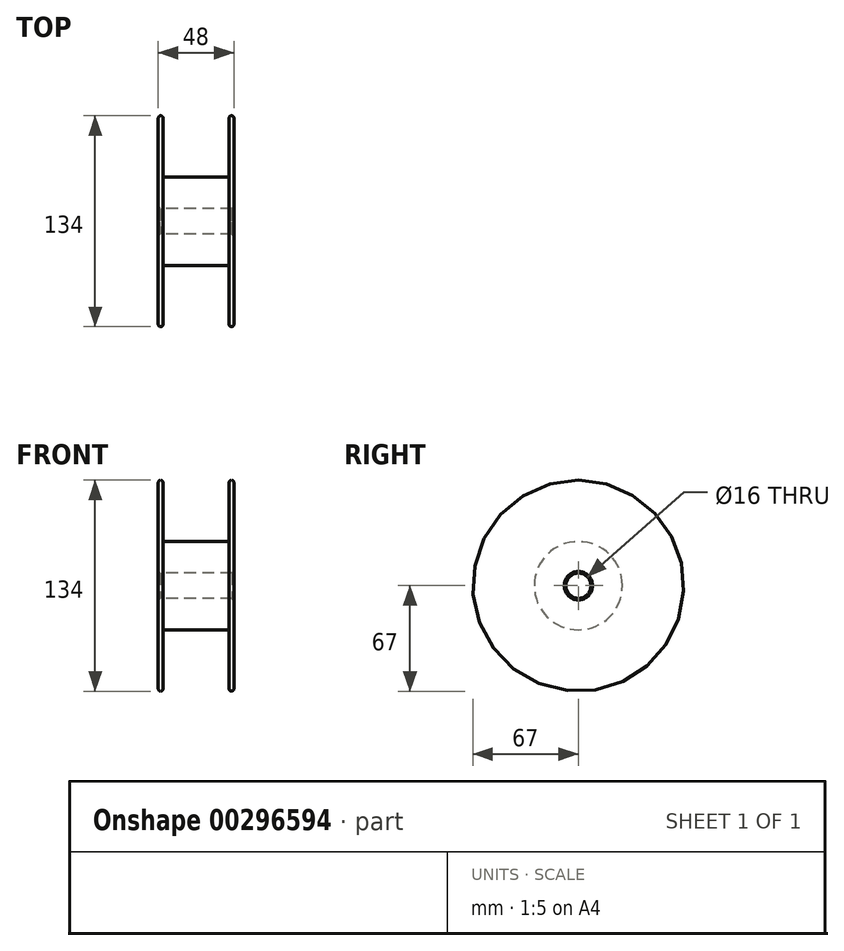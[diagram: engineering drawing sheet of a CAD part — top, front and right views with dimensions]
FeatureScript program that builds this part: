
annotation { "Feature Type Name" : "Feature", "Feature Type Description" : "" }
export const myFeature = defineFeature(function(context is Context, id is Id, definition is map)
    precondition{}
    {
        {
            var Q0;
            Q0=qCreatedBy(makeId("Top.planeOp"),FACE);
            var sketch = newSketch(context, id + "F0", { "sketchPlane" : qUnion([Q0])});
            skLineSegment(sketch, "E0", {"start": v(0, 0) * mm, "end": v(48, 0) * mm, "construction": true});
            skLineSegment(sketch, "E1", {"start": v(0, 8) * mm, "end": v(0, 65.5) * mm});
            skLineSegment(sketch, "E2", {"start": v(48, 8) * mm, "end": v(48, 65.5) * mm});
            skLineSegment(sketch, "E3.0", {"start": v(45, 28) * mm, "end": v(45, 65.5) * mm});
            skLineSegment(sketch, "E4.0", {"start": v(3, 28) * mm, "end": v(3, 65.5) * mm});
            skLineSegment(sketch, "E5", {"start": v(1.5, 67) * mm, "end": v(1.5, 67) * mm});
            skLineSegment(sketch, "E6", {"start": v(46.5, 67) * mm, "end": v(46.5, 67) * mm});
            skLineSegment(sketch, "E7", {"start": v(3, 28) * mm, "end": v(45, 28) * mm});
            skLineSegment(sketch, "E8", {"start": v(0, 8) * mm, "end": v(48, 8) * mm});
            skPoint(sketch, "E9.visualSharp", {"position": v(3, 67) * mm});
            skArc(sketch, "E9.filletArc", {"start": v(3, 65.5) * mm, "mid": v(2.56, 66.56) * mm, "end": v(1.5, 67) * mm});
            skPoint(sketch, "E10.visualSharp", {"position": v(0, 67) * mm});
            skArc(sketch, "E10.filletArc", {"start": v(1.5, 67) * mm, "mid": v(0.44, 66.56) * mm, "end": v(0, 65.5) * mm});
            skPoint(sketch, "E11.visualSharp", {"position": v(45, 67) * mm});
            skArc(sketch, "E11.filletArc", {"start": v(46.5, 67) * mm, "mid": v(45.44, 66.56) * mm, "end": v(45, 65.5) * mm});
            skPoint(sketch, "E12.visualSharp", {"position": v(48, 67) * mm});
            skArc(sketch, "E12.filletArc", {"start": v(48, 65.5) * mm, "mid": v(47.56, 66.56) * mm, "end": v(46.5, 67) * mm});
            skSolve(sketch);
        }
        {
            var Q0;
            Q0 = qSketchRegion(id + "F0", true);
            var Q1;
            Q1=sQuery(id+"F0.wireOp",EDGE,"E0");
            revolve(context, id + "F1", {"entities" : qUnion([Q0]), "axis" : qUnion([Q1]), "revolveType" : RevolveType.FULL});
        }
        {
            var Q0;
            Q0=makeQuery(id+"F1.opRevolve","SWEPT_EDGE",EDGE,{"disambiguationData":[OSD([sQuery(id+"F0.wireOp",EDGE,"E1"),sQuery(id+"F0.wireOp",EDGE,"E8")])]});
            var Q1;
            Q1=makeQuery(id+"F1.opRevolve","SWEPT_EDGE",EDGE,{"disambiguationData":[OSD([sQuery(id+"F0.wireOp",EDGE,"E2"),sQuery(id+"F0.wireOp",EDGE,"E8")])]});
            chamfer(context, id + "F2", {"entities" : qUnion([Q0, Q1]), "width" : 1 * mm, "tangentPropagation" : true});
        }
    });
